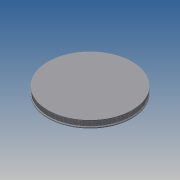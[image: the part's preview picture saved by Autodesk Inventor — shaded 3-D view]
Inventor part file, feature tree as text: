
AUTODESK INVENTOR PART (.ipt)
format: ipt  version: 2013 (Build 170138000, 138)  size: 909,312 bytes
history: native  units: mm
features: extrude x3, sketch x3, pattern_circular x1, chamfer x1, mirror x1
ambient origin geometry x8: Origin, YZ Plane, XZ Plane, XY Plane, X Axis, Y Axis, Z Axis, Center Point
bodies: Solid1 (feature_tree), Solid2 (feature_tree)
feature tree (9):
  extrude  "Extrusion14"  TaperAngle=360.0deg  [1 undecoded]
  extrude  "Extrusion15"  Depth=2.5mm TaperAngle=0.0deg
  pattern_circular  "Circular Pattern1"  [2 undecoded]
  extrude  "Extrusion3"  Depth=8.0mm TaperAngle=0.0deg
  chamfer  "Chamfer2"  Distance=1.59mm
  mirror  "Mirror1"
  sketch  "Sketch3"  dims[d11=0.254mm d20=2350.0mm d21=360.0deg]
  sketch  "Sketch17"  dims[d31=1.0mm d32=2.5mm d33=0.0mm]
  sketch  "Sketch18"  dims[d34=1.0mm d35=2.0mm d36=45.0deg d107=149.097647mm d110=8.0mm d111=0.0mm d112=1.59mm d114=8.0mm d115=0.0mm]
note: 3 required parameter values undecoded (feature->parameter linkage not recoverable at this tier; creation-order binding heuristic only, values carry confidence <= 0.55)
